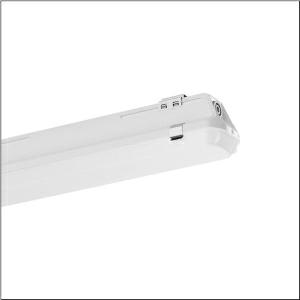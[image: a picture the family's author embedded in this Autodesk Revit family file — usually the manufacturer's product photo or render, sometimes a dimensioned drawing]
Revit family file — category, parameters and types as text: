
# Revit family: monsun_r__21_parking_51fg20dp440bhq_097c
name_source: partatom
category: Lighting Fixtures
units: mm (PartAtom-declared; Revit-internal decimal feet)

## family parameters
Cut with Voids When Loaded = No
Host = Face
Light Source = No
Part Type = Normal
Room Calculation Point = No
Round Connector Dimension = Use Diameter
Shared = No

## types (1)
- --- (1 x LED, 4810 lm, 34.9 W, 4000K)
    Apparent Load = 35 VA
    CIE Flux Codes = 45 75 93 94 100
    Color Rendering = 80
    Color Temperature = 4000K
    Default Elevation = 1800 mm
    Description = Monsun® 21 parking, damp-proof luminaire, chain hanger, primary optical cover: enclosure, of PC, light emission: direct distribution, primary light characteristic: symmetric, installation type: suspended mounting, surface-mounted, horizontal mounting, vertical mounting, LED, rated luminous flux: 4.810lm, luminous efficacy: 140lm/W, light colour: 840, colour temperature: 4000K, control gear: ECG DALI, with terminal, 5-pole, max. 2.5mm², mains connection: 220..240V, AC, 50/60Hz, rated input power: 34W, housing, of glass-fibre reinforced polyester, uncoated, bright grey, incl. chain hanger, length: 1.590mm, width: 90mm, height: 88mm, clip for enclosure, of stainless steel (V2A), ceiling mounting element, of stainless steel (V2A), chain hanger, of stainless steel (V2A), multi-sensor HC1, local controlcentral control, scope of services: certified according to part 101,103,303,304, dimmable, protection rating (complete): IP66, insulation class (complete): insulation class I (protective earthing), certification: CE, ENEC, VDE, UKCA, protection symbol: D, impact resistance: IK08, permissible operating ambient temperature: -25..+35°C, standard: EN 50419, EN 60598-2-1, corresponds to IFS (International Featured Standards) requirements for safety and quality in the food industry, for indoor or canopied outdoor use, no direct snow, no direct sun, no direct rain, contact your sales advisor before using the luminaires in applications with unclear chemical exposure, large temperature fluctuations or condensation-forming humidity, LABS conformity tested according to VDMA 24364:2018-05, packaging unit: 1 piece
    Height = 89 mm
    Lamp = 1 x LED
    Lamp Light Flux = 4810 lm
    Lamp Power = 34.9 W
    Lamp count = 1
    Length = 1590 mm
    Luminous efficacy = 138 lm/W
    Manufacturer = Siteco
    ModVariant = No
    Model = 51FG20DP440BHQ
    Mounting Place = Ceiling
    Mounting Type = Surface mounted
    Number of Poles = 1
    OnlyDefault = Yes
    Power Factor = 1
    Product Name = Monsun® 21 parking
    Product group = damp-proof luminaire
    ProductGroupID = 300
    Protection Class = Protection class I
    Protection Degree = IP 66
    RLX_Detail_Level = 1
    RLX_Emergency_Light_Flux = 0 lm
    RLX_Emergency_Type = 0
    RLX_Emergency_Type_DB = No
    RlxData = <blob elided: 92533 chars, md5=fbf44c19>
    Socket = socket
    Standby Power = 0 W
    System Light Flux = 4810 lm
    System Power = 35 W
    Type Comments = factory setting: luminous flux: 100 % | dim-lin: 254 | 228 mA
    Type Image = l_1006717.jpg
    URL = http://relux.com
    VarID = @adj_074795
    Voltage = 0 V
    Weight = 0.00 kg
    Width = 90 mm

## geometry (parser evidence)
native form markers: Blend x4, Sweep x12
no freeform markers — native parametric forms only
